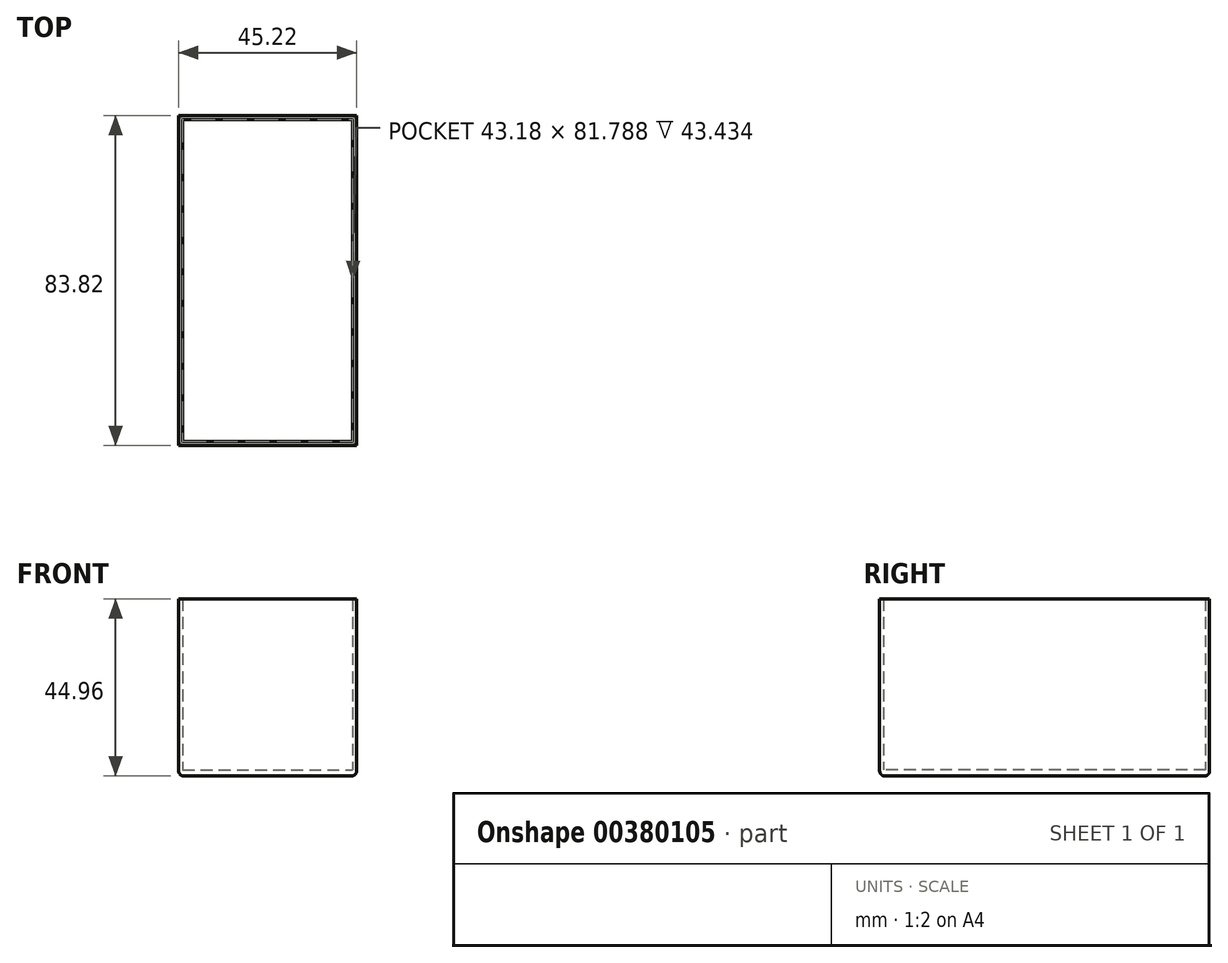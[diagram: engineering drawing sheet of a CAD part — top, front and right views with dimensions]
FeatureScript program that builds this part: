
annotation { "Feature Type Name" : "Feature", "Feature Type Description" : "" }
export const myFeature = defineFeature(function(context is Context, id is Id, definition is map)
    precondition{}
    {
        {
            var Q0;
            Q0=qCreatedBy(makeId("Top.planeOp"),FACE);
            var sketch = newSketch(context, id + "F0", { "sketchPlane" : qUnion([Q0])});
            skLineSegment(sketch, "E0.bottom", {"start": v(-22.6, 41.9) * mm, "end": v(22.6, 41.91) * mm});
            skLineSegment(sketch, "E0.top", {"start": v(-22.6, -41.91) * mm, "end": v(22.6, -41.9) * mm});
            skLineSegment(sketch, "E0.left", {"start": v(-22.6, 41.9) * mm, "end": v(-22.6, -41.91) * mm});
            skLineSegment(sketch, "E0.right", {"start": v(22.6, 41.91) * mm, "end": v(22.6, -41.91) * mm});
            skPoint(sketch, "E0.middle", {"position": v(0, 0) * mm});
            skSolve(sketch);
        }
        {
            var Q0;
            Q0=qSketchRegion(id+"F0",true);
            extrude(context, id + "F1", {"entities" : qUnion([Q0]), "depth" : 1.52 * mm});
        }
        {
            var Q0;
            Q0=makeQuery(id+"F1.opExtrude","CAP_FACE",FACE,{"disambiguationData":[OSD([sQuery(id+"F0.wireOp",EDGE,"E0.bottom"),sQuery(id+"F0.wireOp",EDGE,"E0.top"),sQuery(id+"F0.wireOp",EDGE,"E0.left"),sQuery(id+"F0.wireOp",EDGE,"E0.right")])],"isStart":false});
            var sketch = newSketch(context, id + "F2", { "sketchPlane" : qUnion([Q0])});
            skLineSegment(sketch, "E1.bottom", {"start": v(-21.6, 40.9) * mm, "end": v(21.59, 40.9) * mm});
            skLineSegment(sketch, "E1.top", {"start": v(-21.6, -40.9) * mm, "end": v(21.6, -40.9) * mm});
            skLineSegment(sketch, "E1.left", {"start": v(-21.6, 40.9) * mm, "end": v(-21.6, -40.9) * mm});
            skLineSegment(sketch, "E1.right", {"start": v(21.59, 40.9) * mm, "end": v(21.59, -40.9) * mm});
            skPoint(sketch, "E1.middle", {"position": v(0, 0) * mm});
            skSolve(sketch);
        }
        {
            var Q0;
            Q0=makeQuery(id+"F2.imprint","IMPRINT",FACE,{"disambiguationData":[TD([[makeQuery(id+"F2.imprint","IMPRINT",EDGE,{"derivedFrom":sQuery(id+"F2.wireOp",EDGE,"E1.bottom")}),1.0]])]});
            extrude(context, id + "F3", {"entities" : qUnion([Q0]), "operationType" : NewBodyOperationType.ADD, "depth" : 43.43 * mm});
        }
        {
            var Q0;
            Q0=makeQuery(id+"F1.opExtrude","CAP_FACE",FACE,{"disambiguationData":[OSD([sQuery(id+"F0.wireOp",EDGE,"E0.bottom"),sQuery(id+"F0.wireOp",EDGE,"E0.top"),sQuery(id+"F0.wireOp",EDGE,"E0.left"),sQuery(id+"F0.wireOp",EDGE,"E0.right")])],"isStart":true});
            fillet(context, id + "F4", {"entities" : qUnion([Q0]), "radius" : 1.27 * mm, "tangentPropagation" : true, "allowEdgeOverflow" : false});
        }
    });
